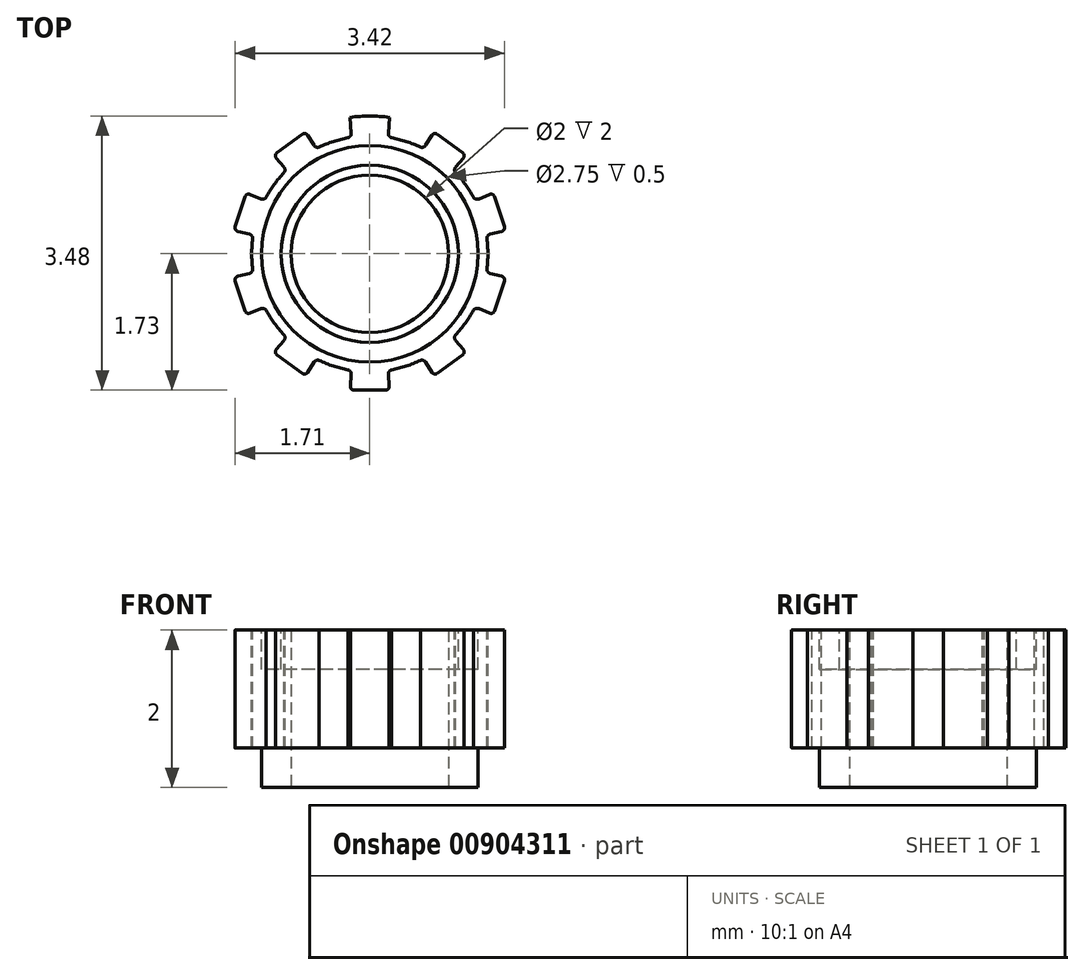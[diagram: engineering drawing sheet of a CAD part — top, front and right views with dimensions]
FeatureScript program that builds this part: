
annotation { "Feature Type Name" : "Feature", "Feature Type Description" : "" }
export const myFeature = defineFeature(function(context is Context, id is Id, definition is map)
    precondition{}
    {
        {
            var Q0;
            Q0=qCreatedBy(makeId("Front.planeOp"),FACE);
            var sketch = newSketch(context, id + "F0", { "sketchPlane" : qUnion([Q0])});
            skLineSegment(sketch, "E0.bottom", {"start": v(0, 0) * mm, "end": v(-1.75, 0) * mm});
            skLineSegment(sketch, "E0.top", {"start": v(0, 2) * mm, "end": v(-1.75, 2) * mm});
            skLineSegment(sketch, "E0.left", {"start": v(0, 0) * mm, "end": v(0, 2) * mm});
            skLineSegment(sketch, "E0.right", {"start": v(-1.75, 0) * mm, "end": v(-1.75, 2) * mm});
            skLineSegment(sketch, "E1", {"start": v(-1, 2) * mm, "end": v(-1, 0) * mm});
            skSolve(sketch);
        }
        {
            var Q0;
            {var subQ0=sQuery(id+"F0.wireOp",EDGE,"E0.right");Q0=makeQuery(id+"F0.imprint","IMPRINT",FACE,{"disambiguationData":[TD([[makeQuery(id+"F0.imprint","IMPRINT",EDGE,{"derivedFrom":subQ0}),-1.0]])]});}
            var Q1;
            Q1=sQuery(id+"F0.wireOp",EDGE,"E0.left");
            revolve(context, id + "F1", {"surfaceOperationType" : NewSurfaceOperationType.NEW, "entities" : qUnion([Q0]), "axis" : qUnion([Q1]), "revolveType" : RevolveType.FULL});
        }
        {
            var Q0;
            Q0=makeQuery(id+"F1.opRevolve","SWEPT_FACE",FACE,{"disambiguationData":[OSD([sQuery(id+"F0.wireOp",EDGE,"E0.top")])]});
            var sketch = newSketch(context, id + "F2", { "sketchPlane" : qUnion([Q0])});
            skLineSegment(sketch, "E2", {"start": v(0, 0) * mm, "end": v(0, 1.75) * mm});
            skLineSegment(sketch, "E3", {"start": v(0, 1.73) * mm, "end": v(-0.25, 1.73) * mm});
            skLineSegment(sketch, "E4", {"start": v(-0.25, 1.73) * mm, "end": v(0.25, 1.73) * mm});
            skLineSegment(sketch, "E5.bottom", {"start": v(0.12, 0) * mm, "end": v(-0.12, 0) * mm});
            skLineSegment(sketch, "E5.top", {"start": v(0.12, 0) * mm, "end": v(-0.12, 0) * mm});
            skLineSegment(sketch, "E5.left", {"start": v(0.12, 0) * mm, "end": v(0.12, 0) * mm});
            skLineSegment(sketch, "E5.right", {"start": v(-0.12, 0) * mm, "end": v(-0.12, 0) * mm});
            skPoint(sketch, "E5.middle", {"position": v(0, 0) * mm});
            skLineSegment(sketch, "E6", {"start": v(-0.25, 1.73) * mm, "end": v(-0.12, 0) * mm});
            skLineSegment(sketch, "E7", {"start": v(0.25, 1.73) * mm, "end": v(0.12, 0) * mm});
            skCircle(sketch, "E8", {"center": v(0, 0) * mm, "radius": 1.5 * mm});
            skLineSegment(sketch, "E9", {"start": v(-0.25, 1.73) * mm, "end": v(-0.2, 1.73) * mm});
            skLineSegment(sketch, "E10", {"start": v(-0.2, 1.73) * mm, "end": v(0.2, 1.73) * mm});
            skLineSegment(sketch, "E11", {"start": v(0.2, 1.73) * mm, "end": v(0.25, 1.73) * mm});
            skLineSegment(sketch, "E12", {"start": v(-0.2, 1.73) * mm, "end": v(-0.12, 0) * mm});
            skLineSegment(sketch, "E13", {"start": v(0.2, 1.73) * mm, "end": v(0.12, 0) * mm});
            skLineSegment(sketch, "E14", {"start": v(-0.25, 1.68) * mm, "end": v(0.25, 1.68) * mm});
            skLineSegment(sketch, "E15", {"start": v(-0.25, 1.68) * mm, "end": v(-0.3, 1.68) * mm});
            skLineSegment(sketch, "E16", {"start": v(0.25, 1.68) * mm, "end": v(0.3, 1.68) * mm});
            skLineSegment(sketch, "E17", {"start": v(-0.3, 1.68) * mm, "end": v(-0.12, 0) * mm});
            skLineSegment(sketch, "E18", {"start": v(0.3, 1.68) * mm, "end": v(0.12, 0) * mm});
            skLineSegment(sketch, "E19", {"start": v(-0.24, 1.53) * mm, "end": v(0.2, 1.53) * mm});
            skLineSegment(sketch, "E20", {"start": v(0.2, 1.53) * mm, "end": v(0.24, 1.53) * mm});
            skLineSegment(sketch, "E21", {"start": v(0.24, 1.53) * mm, "end": v(-0.2, 1.53) * mm});
            skArc(sketch, "E22", {"start": v(-0.28, 1.47) * mm, "mid": v(-0.25, 1.5) * mm, "end": v(-0.24, 1.53) * mm});
            skArc(sketch, "E23", {"start": v(-0.2, 1.73) * mm, "mid": v(-0.23, 1.72) * mm, "end": v(-0.25, 1.68) * mm});
            skArc(sketch, "E24", {"start": v(0.25, 1.68) * mm, "mid": v(0.23, 1.72) * mm, "end": v(0.2, 1.73) * mm});
            skArc(sketch, "E25", {"start": v(0.24, 1.53) * mm, "mid": v(0.25, 1.5) * mm, "end": v(0.28, 1.47) * mm});
            skArc(sketch, "E26.1.0", {"start": v(-1.09, 1.03) * mm, "mid": v(-1.08, 1.07) * mm, "end": v(-1.1, 1.1) * mm});
            skLineSegment(sketch, "E26.1.1", {"start": v(-1.22, 1.25) * mm, "end": v(-0.1, -0.07) * mm});
            skArc(sketch, "E26.1.2", {"start": v(-1.18, 1.28) * mm, "mid": v(-1.2, 1.25) * mm, "end": v(-1.19, 1.22) * mm});
            skLineSegment(sketch, "E26.1.3", {"start": v(-1.22, 1.25) * mm, "end": v(-0.82, 1.55) * mm});
            skArc(sketch, "E26.1.4", {"start": v(-0.79, 1.5) * mm, "mid": v(-0.82, 1.53) * mm, "end": v(-0.86, 1.52) * mm});
            skLineSegment(sketch, "E26.1.5", {"start": v(-0.82, 1.55) * mm, "end": v(0.1, 0.07) * mm});
            skArc(sketch, "E26.1.6", {"start": v(-0.7, 1.38) * mm, "mid": v(-0.68, 1.35) * mm, "end": v(-0.64, 1.35) * mm});
            skArc(sketch, "E26.2.0", {"start": v(-1.49, 0.2) * mm, "mid": v(-1.5, 0.23) * mm, "end": v(-1.53, 0.25) * mm});
            skLineSegment(sketch, "E26.2.1", {"start": v(-1.72, 0.3) * mm, "end": v(-0.04, -0.12) * mm});
            skArc(sketch, "E26.2.2", {"start": v(-1.7, 0.35) * mm, "mid": v(-1.7, 0.3) * mm, "end": v(-1.68, 0.29) * mm});
            skLineSegment(sketch, "E26.2.3", {"start": v(-1.72, 0.3) * mm, "end": v(-1.57, 0.77) * mm});
            skArc(sketch, "E26.2.4", {"start": v(-1.52, 0.75) * mm, "mid": v(-1.56, 0.75) * mm, "end": v(-1.59, 0.73) * mm});
            skLineSegment(sketch, "E26.2.5", {"start": v(-1.57, 0.77) * mm, "end": v(0.04, 0.12) * mm});
            skArc(sketch, "E26.2.6", {"start": v(-1.38, 0.7) * mm, "mid": v(-1.35, 0.7) * mm, "end": v(-1.32, 0.72) * mm});
            skArc(sketch, "E27.2.3.0", {"start": v(-1.32, -0.72) * mm, "mid": v(-1.35, -0.7) * mm, "end": v(-1.38, -0.7) * mm});
            skLineSegment(sketch, "E27.4.3.0", {"start": v(-1.57, -0.77) * mm, "end": v(0.04, -0.12) * mm});
            skArc(sketch, "E27.7.3.0", {"start": v(-1.59, -0.73) * mm, "mid": v(-1.56, -0.75) * mm, "end": v(-1.52, -0.75) * mm});
            skLineSegment(sketch, "E27.11.3.0", {"start": v(-1.57, -0.77) * mm, "end": v(-1.72, -0.3) * mm});
            skArc(sketch, "E27.14.3.0", {"start": v(-1.68, -0.29) * mm, "mid": v(-1.7, -0.3) * mm, "end": v(-1.7, -0.35) * mm});
            skLineSegment(sketch, "E27.18.3.0", {"start": v(-1.72, -0.3) * mm, "end": v(-0.04, 0.12) * mm});
            skArc(sketch, "E27.21.3.0", {"start": v(-1.53, -0.25) * mm, "mid": v(-1.5, -0.23) * mm, "end": v(-1.49, -0.2) * mm});
            skArc(sketch, "E27.2.4.0", {"start": v(-0.64, -1.35) * mm, "mid": v(-0.68, -1.35) * mm, "end": v(-0.7, -1.38) * mm});
            skLineSegment(sketch, "E27.4.4.0", {"start": v(-0.82, -1.55) * mm, "end": v(0.1, -0.07) * mm});
            skArc(sketch, "E27.7.4.0", {"start": v(-0.86, -1.52) * mm, "mid": v(-0.82, -1.53) * mm, "end": v(-0.79, -1.5) * mm});
            skLineSegment(sketch, "E27.11.4.0", {"start": v(-0.82, -1.55) * mm, "end": v(-1.22, -1.25) * mm});
            skArc(sketch, "E27.14.4.0", {"start": v(-1.19, -1.22) * mm, "mid": v(-1.2, -1.25) * mm, "end": v(-1.18, -1.28) * mm});
            skLineSegment(sketch, "E27.18.4.0", {"start": v(-1.22, -1.25) * mm, "end": v(-0.1, 0.07) * mm});
            skArc(sketch, "E27.21.4.0", {"start": v(-1.1, -1.1) * mm, "mid": v(-1.08, -1.07) * mm, "end": v(-1.09, -1.03) * mm});
            skArc(sketch, "E27.2.5.0", {"start": v(0.28, -1.47) * mm, "mid": v(0.25, -1.5) * mm, "end": v(0.24, -1.53) * mm});
            skLineSegment(sketch, "E27.4.5.0", {"start": v(0.25, -1.73) * mm, "end": v(0.13, 0) * mm});
            skArc(sketch, "E27.7.5.0", {"start": v(0.2, -1.73) * mm, "mid": v(0.23, -1.72) * mm, "end": v(0.25, -1.68) * mm});
            skLineSegment(sketch, "E27.11.5.0", {"start": v(0.25, -1.73) * mm, "end": v(-0.25, -1.73) * mm});
            skArc(sketch, "E27.14.5.0", {"start": v(-0.25, -1.68) * mm, "mid": v(-0.23, -1.72) * mm, "end": v(-0.2, -1.73) * mm});
            skLineSegment(sketch, "E27.18.5.0", {"start": v(-0.25, -1.73) * mm, "end": v(-0.13, 0) * mm});
            skArc(sketch, "E27.21.5.0", {"start": v(-0.24, -1.53) * mm, "mid": v(-0.25, -1.5) * mm, "end": v(-0.28, -1.47) * mm});
            skArc(sketch, "E27.2.6.0", {"start": v(1.09, -1.03) * mm, "mid": v(1.08, -1.07) * mm, "end": v(1.1, -1.1) * mm});
            skLineSegment(sketch, "E27.4.6.0", {"start": v(1.22, -1.25) * mm, "end": v(0.1, 0.07) * mm});
            skArc(sketch, "E27.7.6.0", {"start": v(1.18, -1.28) * mm, "mid": v(1.2, -1.25) * mm, "end": v(1.19, -1.22) * mm});
            skLineSegment(sketch, "E27.11.6.0", {"start": v(1.22, -1.25) * mm, "end": v(0.82, -1.55) * mm});
            skArc(sketch, "E27.14.6.0", {"start": v(0.79, -1.5) * mm, "mid": v(0.82, -1.53) * mm, "end": v(0.86, -1.52) * mm});
            skLineSegment(sketch, "E27.18.6.0", {"start": v(0.82, -1.55) * mm, "end": v(-0.1, -0.07) * mm});
            skArc(sketch, "E27.21.6.0", {"start": v(0.7, -1.38) * mm, "mid": v(0.68, -1.35) * mm, "end": v(0.64, -1.35) * mm});
            skArc(sketch, "E27.2.7.0", {"start": v(1.49, -0.2) * mm, "mid": v(1.5, -0.23) * mm, "end": v(1.53, -0.25) * mm});
            skLineSegment(sketch, "E27.4.7.0", {"start": v(1.72, -0.3) * mm, "end": v(0.04, 0.12) * mm});
            skArc(sketch, "E27.7.7.0", {"start": v(1.7, -0.35) * mm, "mid": v(1.7, -0.3) * mm, "end": v(1.68, -0.29) * mm});
            skLineSegment(sketch, "E27.11.7.0", {"start": v(1.72, -0.3) * mm, "end": v(1.57, -0.77) * mm});
            skArc(sketch, "E27.14.7.0", {"start": v(1.52, -0.75) * mm, "mid": v(1.56, -0.75) * mm, "end": v(1.59, -0.73) * mm});
            skLineSegment(sketch, "E27.18.7.0", {"start": v(1.57, -0.77) * mm, "end": v(-0.04, -0.12) * mm});
            skArc(sketch, "E27.21.7.0", {"start": v(1.38, -0.7) * mm, "mid": v(1.35, -0.7) * mm, "end": v(1.32, -0.72) * mm});
            skArc(sketch, "E28.2.8.0", {"start": v(1.32, 0.72) * mm, "mid": v(1.35, 0.7) * mm, "end": v(1.38, 0.7) * mm});
            skLineSegment(sketch, "E28.4.8.0", {"start": v(1.57, 0.77) * mm, "end": v(-0.04, 0.12) * mm});
            skArc(sketch, "E28.7.8.0", {"start": v(1.59, 0.73) * mm, "mid": v(1.56, 0.75) * mm, "end": v(1.52, 0.75) * mm});
            skLineSegment(sketch, "E28.11.8.0", {"start": v(1.57, 0.77) * mm, "end": v(1.72, 0.3) * mm});
            skArc(sketch, "E28.14.8.0", {"start": v(1.68, 0.29) * mm, "mid": v(1.7, 0.3) * mm, "end": v(1.7, 0.35) * mm});
            skLineSegment(sketch, "E28.18.8.0", {"start": v(1.72, 0.3) * mm, "end": v(0.04, -0.12) * mm});
            skArc(sketch, "E28.21.8.0", {"start": v(1.53, 0.25) * mm, "mid": v(1.5, 0.23) * mm, "end": v(1.49, 0.2) * mm});
            skArc(sketch, "E28.2.9.0", {"start": v(0.64, 1.35) * mm, "mid": v(0.68, 1.35) * mm, "end": v(0.7, 1.38) * mm});
            skLineSegment(sketch, "E28.4.9.0", {"start": v(0.82, 1.55) * mm, "end": v(-0.1, 0.07) * mm});
            skArc(sketch, "E28.7.9.0", {"start": v(0.86, 1.52) * mm, "mid": v(0.82, 1.53) * mm, "end": v(0.79, 1.5) * mm});
            skLineSegment(sketch, "E28.11.9.0", {"start": v(0.82, 1.55) * mm, "end": v(1.22, 1.25) * mm});
            skArc(sketch, "E28.14.9.0", {"start": v(1.19, 1.22) * mm, "mid": v(1.2, 1.25) * mm, "end": v(1.18, 1.28) * mm});
            skLineSegment(sketch, "E28.18.9.0", {"start": v(1.22, 1.25) * mm, "end": v(0.1, -0.07) * mm});
            skArc(sketch, "E28.21.9.0", {"start": v(1.1, 1.1) * mm, "mid": v(1.08, 1.07) * mm, "end": v(1.09, 1.03) * mm});
            skSolve(sketch);
        }
        {
            var Q0;
            {var subQ1=sQuery(id+"F2.wireOp",EDGE,"E15");Q0=makeQuery(id+"F2.imprint","IMPRINT",FACE,{"disambiguationData":[TD([[makeQuery(id+"F2.imprint","IMPRINT",EDGE,{"derivedFrom":subQ1}),-1.0]])]});}
            var Q1;
            {var subQ0=sQuery(id+"F2.wireOp",EDGE,"E15");Q1=makeQuery(id+"F2.imprint","IMPRINT",FACE,{"disambiguationData":[TD([[makeQuery(id+"F2.imprint","IMPRINT",EDGE,{"derivedFrom":subQ0}),1.0]])]});}
            var Q2;
            {var subQ0=sQuery(id+"F2.wireOp",EDGE,"E9");Q2=makeQuery(id+"F2.imprint","IMPRINT",FACE,{"disambiguationData":[TD([[makeQuery(id+"F2.imprint","IMPRINT",EDGE,{"derivedFrom":subQ0}),-1.0]])]});}
            var Q3;
            {var subQ5=sQuery(id+"F2.wireOp",EDGE,"E9");Q3=makeQuery(id+"F2.imprint","IMPRINT",FACE,{"disambiguationData":[TD([[makeQuery(id+"F2.imprint","IMPRINT",EDGE,{"derivedFrom":subQ5}),1.0]])]});}
            var Q4;
            {var subQ5=sQuery(id+"F2.wireOp",EDGE,"E11");Q4=makeQuery(id+"F2.imprint","IMPRINT",FACE,{"disambiguationData":[TD([[makeQuery(id+"F2.imprint","IMPRINT",EDGE,{"derivedFrom":subQ5}),1.0]])]});}
            var Q5;
            {var subQ0=sQuery(id+"F2.wireOp",EDGE,"E11");Q5=makeQuery(id+"F2.imprint","IMPRINT",FACE,{"disambiguationData":[TD([[makeQuery(id+"F2.imprint","IMPRINT",EDGE,{"derivedFrom":subQ0}),-1.0]])]});}
            var Q6;
            {var subQ0=sQuery(id+"F2.wireOp",EDGE,"E16");Q6=makeQuery(id+"F2.imprint","IMPRINT",FACE,{"disambiguationData":[TD([[makeQuery(id+"F2.imprint","IMPRINT",EDGE,{"derivedFrom":subQ0}),1.0]])]});}
            var Q7;
            {var subQ0=sQuery(id+"F2.wireOp",EDGE,"E16");Q7=makeQuery(id+"F2.imprint","IMPRINT",FACE,{"disambiguationData":[TD([[makeQuery(id+"F2.imprint","IMPRINT",EDGE,{"derivedFrom":subQ0}),-1.0]])]});}
            var Q8;
            {var subQ3=sQuery(id+"F2.wireOp",EDGE,"E27.7.7.0");Q8=makeQuery(id+"F2.imprint","IMPRINT",FACE,{"disambiguationData":[TD([[makeQuery(id+"F2.imprint","IMPRINT",EDGE,{"derivedFrom":subQ3}),-1.0]])]});}
            var Q9;
            {var subQ0=sQuery(id+"F2.wireOp",EDGE,"E27.11.7.0");var subQ3=makeQuery(id+"F2.imprint","INTERSECT",VERTEX,{"derivedFrom":[sQuery(id+"F2.wireOp",EDGE,"E27.7.7.0"),subQ0]});Q9=makeQuery(id+"F2.imprint","IMPRINT",FACE,{"disambiguationData":[TD([[makeQuery(id+"F2.imprint","IMPRINT",EDGE,{"disambiguationData":[TD([[subQ3,-1.0]])],"derivedFrom":subQ0}),1.0]])]});}
            var Q10;
            {var subQ3=sQuery(id+"F2.wireOp",EDGE,"E27.14.7.0");Q10=makeQuery(id+"F2.imprint","IMPRINT",FACE,{"disambiguationData":[TD([[makeQuery(id+"F2.imprint","IMPRINT",EDGE,{"derivedFrom":subQ3}),-1.0]])]});}
            var Q11;
            {var subQ4=sQuery(id+"F2.wireOp",EDGE,"E27.2.6.0");Q11=makeQuery(id+"F2.imprint","IMPRINT",FACE,{"disambiguationData":[TD([[makeQuery(id+"F2.imprint","IMPRINT",EDGE,{"derivedFrom":subQ4}),1.0]])]});}
            var Q12;
            {var subQ3=sQuery(id+"F2.wireOp",EDGE,"E27.7.6.0");Q12=makeQuery(id+"F2.imprint","IMPRINT",FACE,{"disambiguationData":[TD([[makeQuery(id+"F2.imprint","IMPRINT",EDGE,{"derivedFrom":subQ3}),-1.0]])]});}
            var Q13;
            {var subQ0=sQuery(id+"F2.wireOp",EDGE,"E27.11.6.0");var subQ3=makeQuery(id+"F2.imprint","INTERSECT",VERTEX,{"derivedFrom":[sQuery(id+"F2.wireOp",EDGE,"E27.7.6.0"),subQ0]});Q13=makeQuery(id+"F2.imprint","IMPRINT",FACE,{"disambiguationData":[TD([[makeQuery(id+"F2.imprint","IMPRINT",EDGE,{"disambiguationData":[TD([[subQ3,-1.0]])],"derivedFrom":subQ0}),1.0]])]});}
            var Q14;
            {var subQ1=sQuery(id+"F2.wireOp",EDGE,"E27.2.5.0");Q14=makeQuery(id+"F2.imprint","IMPRINT",FACE,{"disambiguationData":[TD([[makeQuery(id+"F2.imprint","IMPRINT",EDGE,{"derivedFrom":subQ1}),1.0]])]});}
            var Q15;
            {var subQ3=sQuery(id+"F2.wireOp",EDGE,"E27.14.6.0");Q15=makeQuery(id+"F2.imprint","IMPRINT",FACE,{"disambiguationData":[TD([[makeQuery(id+"F2.imprint","IMPRINT",EDGE,{"derivedFrom":subQ3}),-1.0]])]});}
            var Q16;
            {var subQ0=sQuery(id+"F2.wireOp",EDGE,"E27.11.5.0");var subQ3=makeQuery(id+"F2.imprint","INTERSECT",VERTEX,{"derivedFrom":[sQuery(id+"F2.wireOp",EDGE,"E27.7.5.0"),subQ0]});Q16=makeQuery(id+"F2.imprint","IMPRINT",FACE,{"disambiguationData":[TD([[makeQuery(id+"F2.imprint","IMPRINT",EDGE,{"disambiguationData":[TD([[subQ3,-1.0]])],"derivedFrom":subQ0}),1.0]])]});}
            var Q17;
            {var subQ3=sQuery(id+"F2.wireOp",EDGE,"E27.7.5.0");Q17=makeQuery(id+"F2.imprint","IMPRINT",FACE,{"disambiguationData":[TD([[makeQuery(id+"F2.imprint","IMPRINT",EDGE,{"derivedFrom":subQ3}),-1.0]])]});}
            var Q18;
            {var subQ3=sQuery(id+"F2.wireOp",EDGE,"E27.14.5.0");Q18=makeQuery(id+"F2.imprint","IMPRINT",FACE,{"disambiguationData":[TD([[makeQuery(id+"F2.imprint","IMPRINT",EDGE,{"derivedFrom":subQ3}),-1.0]])]});}
            var Q19;
            {var subQ4=sQuery(id+"F2.wireOp",EDGE,"E27.2.4.0");Q19=makeQuery(id+"F2.imprint","IMPRINT",FACE,{"disambiguationData":[TD([[makeQuery(id+"F2.imprint","IMPRINT",EDGE,{"derivedFrom":subQ4}),1.0]])]});}
            var Q20;
            {var subQ3=sQuery(id+"F2.wireOp",EDGE,"E27.7.4.0");Q20=makeQuery(id+"F2.imprint","IMPRINT",FACE,{"disambiguationData":[TD([[makeQuery(id+"F2.imprint","IMPRINT",EDGE,{"derivedFrom":subQ3}),-1.0]])]});}
            var Q21;
            {var subQ0=sQuery(id+"F2.wireOp",EDGE,"E27.11.4.0");var subQ3=makeQuery(id+"F2.imprint","INTERSECT",VERTEX,{"derivedFrom":[sQuery(id+"F2.wireOp",EDGE,"E27.7.4.0"),subQ0]});Q21=makeQuery(id+"F2.imprint","IMPRINT",FACE,{"disambiguationData":[TD([[makeQuery(id+"F2.imprint","IMPRINT",EDGE,{"disambiguationData":[TD([[subQ3,-1.0]])],"derivedFrom":subQ0}),1.0]])]});}
            var Q22;
            {var subQ3=sQuery(id+"F2.wireOp",EDGE,"E27.14.4.0");Q22=makeQuery(id+"F2.imprint","IMPRINT",FACE,{"disambiguationData":[TD([[makeQuery(id+"F2.imprint","IMPRINT",EDGE,{"derivedFrom":subQ3}),-1.0]])]});}
            var Q23;
            {var subQ1=sQuery(id+"F2.wireOp",EDGE,"E27.2.3.0");Q23=makeQuery(id+"F2.imprint","IMPRINT",FACE,{"disambiguationData":[TD([[makeQuery(id+"F2.imprint","IMPRINT",EDGE,{"derivedFrom":subQ1}),1.0]])]});}
            var Q24;
            {var subQ3=sQuery(id+"F2.wireOp",EDGE,"E27.7.3.0");Q24=makeQuery(id+"F2.imprint","IMPRINT",FACE,{"disambiguationData":[TD([[makeQuery(id+"F2.imprint","IMPRINT",EDGE,{"derivedFrom":subQ3}),-1.0]])]});}
            var Q25;
            {var subQ0=sQuery(id+"F2.wireOp",EDGE,"E27.11.3.0");var subQ3=makeQuery(id+"F2.imprint","INTERSECT",VERTEX,{"derivedFrom":[sQuery(id+"F2.wireOp",EDGE,"E27.7.3.0"),subQ0]});Q25=makeQuery(id+"F2.imprint","IMPRINT",FACE,{"disambiguationData":[TD([[makeQuery(id+"F2.imprint","IMPRINT",EDGE,{"disambiguationData":[TD([[subQ3,-1.0]])],"derivedFrom":subQ0}),1.0]])]});}
            var Q26;
            {var subQ3=sQuery(id+"F2.wireOp",EDGE,"E27.14.3.0");Q26=makeQuery(id+"F2.imprint","IMPRINT",FACE,{"disambiguationData":[TD([[makeQuery(id+"F2.imprint","IMPRINT",EDGE,{"derivedFrom":subQ3}),-1.0]])]});}
            var Q27;
            {var subQ0=sQuery(id+"F2.wireOp",EDGE,"E26.2.3");var subQ3=makeQuery(id+"F2.imprint","INTERSECT",VERTEX,{"derivedFrom":[sQuery(id+"F2.wireOp",EDGE,"E26.2.2"),subQ0]});Q27=makeQuery(id+"F2.imprint","IMPRINT",FACE,{"disambiguationData":[TD([[makeQuery(id+"F2.imprint","IMPRINT",EDGE,{"disambiguationData":[TD([[subQ3,-1.0]])],"derivedFrom":subQ0}),1.0]])]});}
            var Q28;
            {var subQ3=sQuery(id+"F2.wireOp",EDGE,"E26.2.2");Q28=makeQuery(id+"F2.imprint","IMPRINT",FACE,{"disambiguationData":[TD([[makeQuery(id+"F2.imprint","IMPRINT",EDGE,{"derivedFrom":subQ3}),-1.0]])]});}
            var Q29;
            {var subQ1=sQuery(id+"F2.wireOp",EDGE,"E26.2.0");Q29=makeQuery(id+"F2.imprint","IMPRINT",FACE,{"disambiguationData":[TD([[makeQuery(id+"F2.imprint","IMPRINT",EDGE,{"derivedFrom":subQ1}),1.0]])]});}
            var Q30;
            {var subQ3=sQuery(id+"F2.wireOp",EDGE,"E26.2.4");Q30=makeQuery(id+"F2.imprint","IMPRINT",FACE,{"disambiguationData":[TD([[makeQuery(id+"F2.imprint","IMPRINT",EDGE,{"derivedFrom":subQ3}),-1.0]])]});}
            var Q31;
            {var subQ1=sQuery(id+"F2.wireOp",EDGE,"E26.1.0");Q31=makeQuery(id+"F2.imprint","IMPRINT",FACE,{"disambiguationData":[TD([[makeQuery(id+"F2.imprint","IMPRINT",EDGE,{"derivedFrom":subQ1}),1.0]])]});}
            var Q32;
            {var subQ3=sQuery(id+"F2.wireOp",EDGE,"E26.1.2");Q32=makeQuery(id+"F2.imprint","IMPRINT",FACE,{"disambiguationData":[TD([[makeQuery(id+"F2.imprint","IMPRINT",EDGE,{"derivedFrom":subQ3}),-1.0]])]});}
            var Q33;
            {var subQ3=sQuery(id+"F2.wireOp",EDGE,"E26.1.4");Q33=makeQuery(id+"F2.imprint","IMPRINT",FACE,{"disambiguationData":[TD([[makeQuery(id+"F2.imprint","IMPRINT",EDGE,{"derivedFrom":subQ3}),-1.0]])]});}
            var Q34;
            {var subQ0=sQuery(id+"F2.wireOp",EDGE,"E26.1.3");var subQ3=makeQuery(id+"F2.imprint","INTERSECT",VERTEX,{"derivedFrom":[sQuery(id+"F2.wireOp",EDGE,"E26.1.2"),subQ0]});Q34=makeQuery(id+"F2.imprint","IMPRINT",FACE,{"disambiguationData":[TD([[makeQuery(id+"F2.imprint","IMPRINT",EDGE,{"disambiguationData":[TD([[subQ3,-1.0]])],"derivedFrom":subQ0}),1.0]])]});}
            var Q35;
            {var subQ1=sQuery(id+"F2.wireOp",EDGE,"E27.2.7.0");Q35=makeQuery(id+"F2.imprint","IMPRINT",FACE,{"disambiguationData":[TD([[makeQuery(id+"F2.imprint","IMPRINT",EDGE,{"derivedFrom":subQ1}),1.0]])]});}
            var Q36;
            {var subQ3=sQuery(id+"F2.wireOp",EDGE,"E28.14.8.0");Q36=makeQuery(id+"F2.imprint","IMPRINT",FACE,{"disambiguationData":[TD([[makeQuery(id+"F2.imprint","IMPRINT",EDGE,{"derivedFrom":subQ3}),-1.0]])]});}
            var Q37;
            {var subQ0=sQuery(id+"F2.wireOp",EDGE,"E28.11.8.0");var subQ3=makeQuery(id+"F2.imprint","INTERSECT",VERTEX,{"derivedFrom":[sQuery(id+"F2.wireOp",EDGE,"E28.7.8.0"),subQ0]});Q37=makeQuery(id+"F2.imprint","IMPRINT",FACE,{"disambiguationData":[TD([[makeQuery(id+"F2.imprint","IMPRINT",EDGE,{"disambiguationData":[TD([[subQ3,-1.0]])],"derivedFrom":subQ0}),1.0]])]});}
            var Q38;
            {var subQ3=sQuery(id+"F2.wireOp",EDGE,"E28.7.8.0");Q38=makeQuery(id+"F2.imprint","IMPRINT",FACE,{"disambiguationData":[TD([[makeQuery(id+"F2.imprint","IMPRINT",EDGE,{"derivedFrom":subQ3}),-1.0]])]});}
            var Q39;
            {var subQ1=sQuery(id+"F2.wireOp",EDGE,"E28.2.8.0");Q39=makeQuery(id+"F2.imprint","IMPRINT",FACE,{"disambiguationData":[TD([[makeQuery(id+"F2.imprint","IMPRINT",EDGE,{"derivedFrom":subQ1}),1.0]])]});}
            var Q40;
            {var subQ3=sQuery(id+"F2.wireOp",EDGE,"E28.14.9.0");Q40=makeQuery(id+"F2.imprint","IMPRINT",FACE,{"disambiguationData":[TD([[makeQuery(id+"F2.imprint","IMPRINT",EDGE,{"derivedFrom":subQ3}),-1.0]])]});}
            var Q41;
            {var subQ0=sQuery(id+"F2.wireOp",EDGE,"E28.11.9.0");var subQ3=makeQuery(id+"F2.imprint","INTERSECT",VERTEX,{"derivedFrom":[sQuery(id+"F2.wireOp",EDGE,"E28.7.9.0"),subQ0]});Q41=makeQuery(id+"F2.imprint","IMPRINT",FACE,{"disambiguationData":[TD([[makeQuery(id+"F2.imprint","IMPRINT",EDGE,{"disambiguationData":[TD([[subQ3,-1.0]])],"derivedFrom":subQ0}),1.0]])]});}
            var Q42;
            {var subQ3=sQuery(id+"F2.wireOp",EDGE,"E28.7.9.0");Q42=makeQuery(id+"F2.imprint","IMPRINT",FACE,{"disambiguationData":[TD([[makeQuery(id+"F2.imprint","IMPRINT",EDGE,{"derivedFrom":subQ3}),-1.0]])]});}
            extrude(context, id + "F3", {"entities" : qUnion([Q0, Q1, Q2, Q3, Q4, Q5, Q6, Q7, Q8, Q9, Q10, Q11, Q12, Q13, Q14, Q15, Q16, Q17, Q18, Q19, Q20, Q21, Q22, Q23, Q24, Q25, Q26, Q27, Q28, Q29, Q30, Q31, Q32, Q33, Q34, Q35, Q36, Q37, Q38, Q39, Q40, Q41, Q42]), "operationType" : NewBodyOperationType.REMOVE, "oppositeDirection" : true, "depth" : 25 * mm, "offsetDistance" : 25 * mm});
        }
        {
            var Q0;
            Q0=makeQuery(id+"F1.opRevolve","SWEPT_FACE",FACE,{"disambiguationData":[OSD([sQuery(id+"F0.wireOp",EDGE,"E0.top")])]});
            var sketch = newSketch(context, id + "F4", { "sketchPlane" : qUnion([Q0])});
            skCircle(sketch, "E29", {"center": v(0, 0) * mm, "radius": 1.13 * mm});
            skCircle(sketch, "E30", {"center": v(0, 0) * mm, "radius": 1.38 * mm});
            skSolve(sketch);
        }
        {
            var Q0;
            Q0=makeQuery(id+"F1.opRevolve","SWEPT_FACE",FACE,{"disambiguationData":[OSD([sQuery(id+"F0.wireOp",EDGE,"E0.bottom")])]});
            var sketch = newSketch(context, id + "F5", { "sketchPlane" : qUnion([Q0])});
            skCircle(sketch, "E31.0", {"center": v(0, 0) * mm, "radius": 1.38 * mm});
            skCircle(sketch, "E31.1", {"center": v(0, 0) * mm, "radius": 1.13 * mm});
            skSolve(sketch);
        }
        {
            var Q0;
            Q0=makeQuery(id+"F5.imprint","IMPRINT",FACE,{"disambiguationData":[TD([[makeQuery(id+"F5.imprint","IMPRINT",EDGE,{"derivedFrom":sQuery(id+"F5.wireOp",EDGE,"E31.0")}),-1.0]])]});
            extrude(context, id + "F6", {"entities" : qUnion([Q0]), "operationType" : NewBodyOperationType.REMOVE, "oppositeDirection" : true, "depth" : 0.5 * mm, "offsetDistance" : 25 * mm});
        }
        {
            var Q0;
            Q0=makeQuery(id+"F4.imprint","IMPRINT",FACE,{"disambiguationData":[TD([[makeQuery(id+"F4.imprint","IMPRINT",EDGE,{"derivedFrom":sQuery(id+"F4.wireOp",EDGE,"E29")}),-1.0]])]});
            extrude(context, id + "F7", {"entities" : qUnion([Q0]), "operationType" : NewBodyOperationType.REMOVE, "oppositeDirection" : true, "depth" : 0.5 * mm, "offsetDistance" : 25 * mm});
        }
    });
